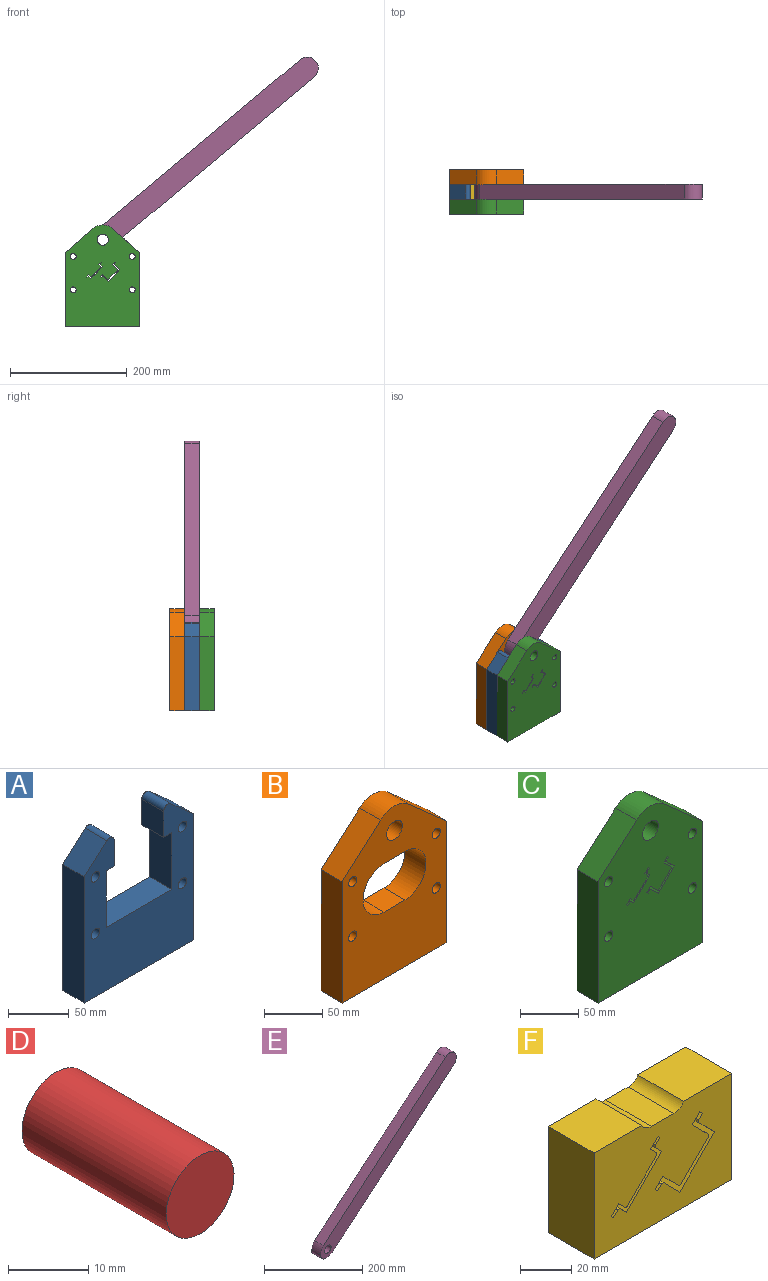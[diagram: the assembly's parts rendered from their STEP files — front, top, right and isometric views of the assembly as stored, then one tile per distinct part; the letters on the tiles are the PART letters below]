
ASSEMBLY  parts=6 mates=5
PART A: 20 faces, bbox 127x25.4x151.6 mm
  f0: plane 76.45x25.4mm, normal (0,0,1), area 1941.9mm2, adj f1,f9,f10,f11
  f1: plane 57.15x25.4mm, normal (1,0,0), area 1451.6mm2, adj f0,f2,f10,f11
  f2: plane 25.4x9.53mm, normal (0,0,-1), area 241.9mm2, adj f1,f3,f10,f11
  f3: plane 25.84x25.4mm, normal (1,0,0), area 656.2mm2, adj f2,f10,f11,f14
  f4: plane 127x25.4mm, normal (-1,0,0), area 3225.8mm2, adj f5,f10,f11,f15
  f5: plane 127x25.4mm, normal (0,0,-1), area 3225.8mm2, adj f4,f6,f10,f11
  f6: plane 127x25.4mm, normal (1,0,0), area 3225.8mm2, adj f5,f10,f11,f12
  f7: plane 25.84x25.4mm, normal (-1,0,0), area 656.2mm2, adj f8,f10,f11,f13
  f8: plane 25.4x9.53mm, normal (0,0,-1), area 241.9mm2, adj f7,f9,f10,f11
  f9: plane 57.15x25.4mm, normal (-1,0,0), area 1451.6mm2, adj f0,f8,f10,f11
  f10: plane 151.57x127mm, normal (0,-1,0), area 12101.8mm2, adj f0,f1,f2,f3,f4,f5,f6,f7
  f11: plane 151.57x127mm, normal (0,1,0), area 12101.8mm2, adj f0,f1,f2,f3,f4,f5,f6,f7
  f12: plane 26.35x25.4mm, normal (0.66,0,0.75), area 893.4mm2, adj f6,f10,f11,f13
  f13: cylinder r=5.08mm len=25.4mm, axis (0,1,0), area 296.1mm2, adj f7,f10,f11,f12
  f14: cylinder r=5.08mm len=25.4mm, axis (0,1,0), area 296.1mm2, adj f3,f10,f11,f15
  f15: plane 26.35x25.4mm, normal (-0.66,0,0.75), area 893.4mm2, adj f4,f10,f11,f14
  f16: cylinder r=4.95mm len=25.4mm, axis (0,1,0), area 790.5mm2, adj f10,f11
  f17: cylinder r=4.95mm len=25.4mm, axis (0,1,0), area 790.5mm2, adj f10,f11
  f18: cylinder r=4.95mm len=25.4mm, axis (0,1,0), area 790.5mm2, adj f10,f11
  f19: cylinder r=4.95mm len=25.4mm, axis (0,1,0), area 790.5mm2, adj f10,f11
PART B: 17 faces, bbox 127x25.4x174.6 mm
  f0: plane 127x25.4mm, normal (1,0,0), area 3225.8mm2, adj f1,f6,f7,f8
  f1: plane 46.68x41.26mm, normal (0.66,0,0.75), area 1582.4mm2, adj f0,f2,f7,f8
  f2: cylinder r=25.4mm len=33.64mm, axis (0,-1,0), area 934mm2, adj f1,f3,f7,f8
  f3: plane 46.68x41.26mm, normal (-0.66,0,0.75), area 1582.4mm2, adj f2,f4,f7,f8
  f4: plane 127x25.4mm, normal (-1,0,0), area 3225.8mm2, adj f3,f6,f7,f8
  f5: cylinder r=9.53mm len=25.4mm, axis (0,-1,0), area 1520.1mm2, adj f7,f8
  f6: plane 127x25.4mm, normal (0,0,-1), area 3225.8mm2, adj f0,f4,f7,f8
  f7: plane 174.63x127mm, normal (0,1,0), area 15679.2mm2, adj f0,f1,f2,f3,f4,f5,f6,f9
  f8: plane 174.63x127mm, normal (0,-1,0), area 15679.2mm2, adj f0,f1,f2,f3,f4,f5,f6,f9
  f9: plane 25.4x25.4mm, normal (0,0,-1), area 645.2mm2, adj f7,f8,f10,f12
  f10: cylinder r=25.4mm len=50.8mm, axis (0,1,0), area 2026.8mm2, adj f7,f8,f9,f11
  f11: plane 25.4x25.4mm, normal (0,0,1), area 645.2mm2, adj f7,f8,f10,f12
  f12: cylinder r=25.4mm len=50.8mm, axis (0,1,0), area 2026.8mm2, adj f7,f8,f9,f11
  f13: cylinder r=4.95mm len=25.4mm, axis (0,1,0), area 790.5mm2, adj f7,f8
  f14: cylinder r=4.95mm len=25.4mm, axis (0,1,0), area 790.5mm2, adj f7,f8
  f15: cylinder r=4.95mm len=25.4mm, axis (0,1,0), area 790.5mm2, adj f7,f8
  f16: cylinder r=4.95mm len=25.4mm, axis (0,1,0), area 790.5mm2, adj f7,f8
PART C: 45 faces, bbox 127x25.4x174.6 mm
  f0: plane 174.63x127mm, normal (0,-1,0), area 18795.9mm2, adj f2,f3,f4,f5,f6,f7,f8,f9
  f1: plane 174.63x127mm, normal (0,1,0), area 18795.9mm2, adj f2,f3,f4,f5,f6,f7,f8,f9
  f2: plane 127x25.4mm, normal (1,0,0), area 3225.8mm2, adj f0,f1,f3,f8
  f3: plane 46.68x41.26mm, normal (0.66,0,0.75), area 1582.4mm2, adj f0,f1,f2,f4
  f4: cylinder r=25.4mm len=33.64mm, axis (0,1,0), area 934mm2, adj f0,f1,f3,f5
  f5: plane 46.68x41.26mm, normal (-0.66,0,0.75), area 1582.4mm2, adj f0,f1,f4,f6
  f6: plane 127x25.4mm, normal (-1,0,0), area 3225.8mm2, adj f0,f1,f5,f8
  f7: cylinder r=9.53mm len=25.4mm, axis (0,1,0), area 1520.1mm2, adj f0,f1
  f8: plane 127x25.4mm, normal (0,0,-1), area 3225.8mm2, adj f0,f1,f2,f6
  f9: plane 25.4x19.26mm, normal (-0.71,0,0.71), area 691.9mm2, adj f0,f1,f10,f20
  f10: plane 25.4x8.71mm, normal (-0.71,0,-0.71), area 312.9mm2, adj f0,f1,f9,f40
  f11: plane 25.4x2.07mm, normal (-0.71,0,0.71), area 74.2mm2, adj f0,f1,f12,f40
  f12: plane 25.4x1.44mm, normal (-0.71,0,-0.71), area 51.6mm2, adj f0,f1,f11,f13
  f13: plane 25.4x4.22mm, normal (0.71,0,-0.71), area 151.6mm2, adj f0,f1,f12,f14
  f14: plane 25.4x8.71mm, normal (0.71,0,0.71), area 312.9mm2, adj f0,f1,f13,f39
  f15: plane 25.4x14.95mm, normal (0.71,0,-0.71), area 537.1mm2, adj f0,f1,f38,f39
  f16: plane 25.4x8.71mm, normal (-0.71,0,-0.71), area 312.9mm2, adj f0,f1,f17,f38
  f17: plane 25.4x4.22mm, normal (0.71,0,-0.71), area 151.6mm2, adj f0,f1,f16,f18
  f18: plane 25.4x1.44mm, normal (0.71,0,0.71), area 51.6mm2, adj f0,f1,f17,f19
  f19: plane 25.4x2.07mm, normal (-0.71,0,0.71), area 74.2mm2, adj f0,f1,f18,f37
  f20: plane 25.4x8.71mm, normal (0.71,0,0.71), area 312.9mm2, adj f0,f1,f9,f37
  f21: plane 25.4x4.22mm, normal (0.71,0,-0.71), area 151.6mm2, adj f0,f1,f22,f32
  f22: plane 25.4x1.08mm, normal (0.71,0,0.71), area 38.7mm2, adj f0,f1,f21,f23
  f23: plane 25.4x2.42mm, normal (-0.71,0,0.71), area 87.1mm2, adj f0,f1,f22,f33
  f24: plane 25.4x3.32mm, normal (0.71,0,0.71), area 119.4mm2, adj f0,f1,f25,f33
  f25: plane 25.4x19.54mm, normal (-0.71,0,0.71), area 701.9mm2, adj f0,f1,f24,f26
  f26: plane 25.4x3.32mm, normal (-0.71,0,-0.71), area 119.4mm2, adj f0,f1,f25,f34
  f27: plane 25.4x2.42mm, normal (-0.71,0,0.71), area 87.1mm2, adj f0,f1,f28,f34
  f28: plane 25.4x1.08mm, normal (-0.71,0,-0.71), area 38.7mm2, adj f0,f1,f27,f29
  f29: plane 25.4x4.22mm, normal (0.71,0,-0.71), area 151.6mm2, adj f0,f1,f28,f30
  f30: plane 25.4x3.32mm, normal (0.71,0,0.71), area 119.4mm2, adj f0,f1,f29,f35
  f31: plane 25.4x15.95mm, normal (0.71,0,-0.71), area 572.9mm2, adj f0,f1,f35,f36
  f32: plane 25.4x3.32mm, normal (-0.71,0,-0.71), area 119.4mm2, adj f0,f1,f21,f36
  f33: cylinder r=1.02mm len=25.4mm, axis (0,1,0), area 40.5mm2, adj f0,f1,f23,f24
  f34: cylinder r=1.02mm len=25.4mm, axis (0,1,0), area 40.5mm2, adj f0,f1,f26,f27
  f35: cylinder r=1.02mm len=25.4mm, axis (0,1,0), area 40.5mm2, adj f0,f1,f30,f31
  f36: cylinder r=1.02mm len=25.4mm, axis (0,1,0), area 40.5mm2, adj f0,f1,f31,f32
  f37: cylinder r=1.02mm len=25.4mm, axis (0,1,0), area 40.5mm2, adj f0,f1,f19,f20
  f38: cylinder r=1.02mm len=25.4mm, axis (0,1,0), area 40.5mm2, adj f0,f1,f15,f16
  f39: cylinder r=1.02mm len=25.4mm, axis (0,1,0), area 40.5mm2, adj f0,f1,f14,f15
  f40: cylinder r=1.02mm len=25.4mm, axis (0,1,0), area 40.5mm2, adj f0,f1,f10,f11
  f41: cylinder r=4.95mm len=25.4mm, axis (0,1,0), area 790.5mm2, adj f0,f1
  f42: cylinder r=4.95mm len=25.4mm, axis (0,1,0), area 790.5mm2, adj f0,f1
  f43: cylinder r=4.95mm len=25.4mm, axis (0,1,0), area 790.5mm2, adj f0,f1
  f44: cylinder r=4.95mm len=25.4mm, axis (0,1,0), area 790.5mm2, adj f0,f1
PART D: 3 faces, bbox 11.9x25.4x11.9 mm
  f0: cylinder r=5.97mm len=25.4mm, axis (0,1,0), area 952.6mm2, adj f1,f2
  f1: plane 11.94x11.94mm, normal (0,-1,0), area 111.9mm2, adj f0
  f2: plane 11.94x11.94mm, normal (0,1,0), area 111.9mm2, adj f0
PART E: 9 faces, bbox 390x25.4x332.6 mm
  f0: plane 350.24x293.88mm, normal (0.64,0,-0.77), area 11612.9mm2, adj f1,f5,f7,f8
  f1: cylinder r=19.05mm len=33.64mm, axis (0,1,0), area 1520.1mm2, adj f0,f2,f7,f8
  f2: plane 350.24x293.88mm, normal (-0.64,0,0.77), area 11612.9mm2, adj f1,f3,f7,f8
  f3: cylinder r=36.37mm len=25.4mm, axis (0,1,0), area 494.7mm2, adj f2,f4,f7,f8
  f4: cylinder r=14.39mm len=25.4mm, axis (0,1,0), area 637.8mm2, adj f3,f5,f7,f8
  f5: cylinder r=36.37mm len=25.4mm, axis (0,1,0), area 494.7mm2, adj f0,f4,f7,f8
  f6: cylinder r=9.53mm len=25.4mm, axis (0,1,0), area 1520.1mm2, adj f7,f8
  f7: plane 389.99x332.62mm, normal (0,-1,0), area 18342.4mm2, adj f0,f1,f2,f3,f4,f5,f6
  f8: plane 389.99x332.62mm, normal (0,1,0), area 18342.4mm2, adj f0,f1,f2,f3,f4,f5,f6
PART F: 42 faces, bbox 76.2x25.4x50.8 mm
  f0: plane 26.44x25.4mm, normal (0,0,1), area 671.4mm2, adj f1,f26,f30,f31
  f1: plane 76.2x50.8mm, normal (0,1,0), area 3607mm2, adj f0,f2,f3,f4,f5,f6,f7,f8
  f2: plane 25.4x1.08mm, normal (0.71,0,0.71), area 38.7mm2, adj f1,f3,f29,f30
  f3: plane 25.4x4.22mm, normal (0.71,0,-0.71), area 151.6mm2, adj f1,f2,f4,f30
  f4: plane 25.4x3.32mm, normal (-0.71,0,-0.71), area 119.4mm2, adj f1,f3,f30,f38
  f5: plane 25.4x15.95mm, normal (0.71,0,-0.71), area 572.9mm2, adj f1,f30,f38,f39
  f6: plane 25.4x3.32mm, normal (0.71,0,0.71), area 119.4mm2, adj f1,f7,f30,f39
  f7: plane 25.4x4.22mm, normal (0.71,0,-0.71), area 151.6mm2, adj f1,f6,f8,f30
  f8: plane 25.4x1.08mm, normal (-0.71,0,-0.71), area 38.7mm2, adj f1,f7,f9,f30
  f9: plane 25.4x2.42mm, normal (-0.71,0,0.71), area 87.1mm2, adj f1,f8,f30,f40
  f10: plane 25.4x3.32mm, normal (-0.71,0,-0.71), area 119.4mm2, adj f1,f11,f30,f40
  f11: plane 25.4x19.54mm, normal (-0.71,0,0.71), area 701.9mm2, adj f1,f10,f12,f30
  f12: plane 25.4x3.32mm, normal (0.71,0,0.71), area 119.4mm2, adj f1,f11,f30,f41
  f13: plane 25.4x8.71mm, normal (-0.71,0,-0.71), area 312.9mm2, adj f1,f14,f30,f37
  f14: plane 25.4x19.26mm, normal (-0.71,0,0.71), area 691.9mm2, adj f1,f13,f15,f30
  f15: plane 25.4x8.71mm, normal (0.71,0,0.71), area 312.9mm2, adj f1,f14,f30,f34
  f16: plane 25.4x2.07mm, normal (-0.71,0,0.71), area 74.2mm2, adj f1,f17,f30,f34
  f17: plane 25.4x1.44mm, normal (0.71,0,0.71), area 51.6mm2, adj f1,f16,f18,f30
  f18: plane 25.4x4.22mm, normal (0.71,0,-0.71), area 151.6mm2, adj f1,f17,f19,f30
  f19: plane 25.4x8.71mm, normal (-0.71,0,-0.71), area 312.9mm2, adj f1,f18,f30,f35
  f20: plane 25.4x14.95mm, normal (0.71,0,-0.71), area 537.1mm2, adj f1,f30,f35,f36
  f21: plane 25.4x8.71mm, normal (0.71,0,0.71), area 312.9mm2, adj f1,f22,f30,f36
  f22: plane 25.4x4.22mm, normal (0.71,0,-0.71), area 151.6mm2, adj f1,f21,f23,f30
  f23: plane 25.4x1.44mm, normal (-0.71,0,-0.71), area 51.6mm2, adj f1,f22,f27,f30
  f24: plane 50.8x25.4mm, normal (1,0,0), area 1290.3mm2, adj f1,f25,f28,f30
  f25: plane 26.67x25.4mm, normal (0,0,1), area 677.4mm2, adj f1,f24,f30,f33
  f26: plane 50.8x25.4mm, normal (-1,0,0), area 1290.3mm2, adj f0,f1,f28,f30
  f27: plane 25.4x2.07mm, normal (-0.71,0,0.71), area 74.2mm2, adj f1,f23,f30,f37
  f28: plane 76.2x25.4mm, normal (0,0,-1), area 1935.5mm2, adj f1,f24,f26,f30
  f29: plane 25.4x2.42mm, normal (-0.71,0,0.71), area 87.1mm2, adj f1,f2,f30,f41
  f30: plane 76.2x50.8mm, normal (0,-1,0), area 3607mm2, adj f0,f2,f3,f4,f5,f6,f7,f8
  f31: cylinder r=6.1mm len=25.4mm, axis (0,-1,0), area 165.8mm2, adj f0,f1,f30,f32
  f32: plane 25.4x12.4mm, normal (0,0,1), area 314.8mm2, adj f1,f30,f31,f33
  f33: cylinder r=6.1mm len=25.4mm, axis (0,-1,0), area 165.8mm2, adj f1,f25,f30,f32
  f34: cylinder r=1.02mm len=25.4mm, axis (0,1,0), area 40.5mm2, adj f1,f15,f16,f30
  f35: cylinder r=1.02mm len=25.4mm, axis (0,1,0), area 40.5mm2, adj f1,f19,f20,f30
  f36: cylinder r=1.02mm len=25.4mm, axis (0,1,0), area 40.5mm2, adj f1,f20,f21,f30
  f37: cylinder r=1.02mm len=25.4mm, axis (0,1,0), area 40.5mm2, adj f1,f13,f27,f30
  f38: cylinder r=1.02mm len=25.4mm, axis (0,1,0), area 40.5mm2, adj f1,f4,f5,f30
  f39: cylinder r=1.02mm len=25.4mm, axis (0,1,0), area 40.5mm2, adj f1,f5,f6,f30
  f40: cylinder r=1.02mm len=25.4mm, axis (0,1,0), area 40.5mm2, adj f1,f9,f10,f30
  f41: cylinder r=1.02mm len=25.4mm, axis (0,1,0), area 40.5mm2, adj f1,f12,f29,f30
PLACE A at identity fixed
PLACE B at identity fixed
PLACE C at identity
PLACE D rot(axis=(0,1,0),2deg) t=(-1.11,0,-0.22)mm
PLACE E rot(axis=(0,1,0.02),0deg) t=(0,0,0)mm
PLACE F rot(axis=(0,-1,0),0deg) t=(-0.13,0,0.1)mm
MATE planar F.f1 <-> B.f8  axis (0,1,0) through (-0.38,0,-0.2)mm
MATE revolute B.f5 <-> E.f6  axis (0,-1,0) through (0,0,53.98)mm
MATE fastened C.f8 <-> A.f5  axis (0,0,1) through (63.5,-25.4,-95.25)mm
MATE planar D.f0 <-> A.f10  axis (0,-1,0) through (-6.45,-25.4,28.3)mm
MATE planar F.f26 <-> A.f1  axis (-1,0,0) through (-38.23,-12.7,0.1)mm
